# Revit family: Unterlegplatte_PLF_41_8_10_12_ FT_FTK
name_source: partatom
category: Generic Models
revit_build: Autodesk Revit 2017 (Build: 20160225_1515(x64)
units: mm (PartAtom-declared; Revit-internal decimal feet)

## family parameters
Always vertical = Yes
Can host rebar = No
Cut with Voids When Loaded = No
Part Type = Normal
Room Calculation Point = No
Round Connector Dimension = Use Diameter
Shared = No
Work Plane-Based = No

## types (4) — shared parameters
Manufacturer = OBO Bettermann
URL = http:/www.obo-bettermann.com

## per-type parameters (varying)
| type | Diameter | GTIN | Manufacturer Art.No. | Material |
| PLF 41 8 FT | 9 mm  [stored 0.0295276 ft] | 4012196675289 | 7207052 | Hot-dip galvanised |
| PLF 41 10 FT | 12 mm  [stored 0.0393701 ft] | 4012196675296 | 7207054 | Hot-dip galvanised |
| PLF 41 12 FT | 13 mm | 4012196675302 | 7207056 | Hot-dip galvanised |
| WBDHE 41 FTK | 12 mm  [stored 0.0393701 ft] | 4012196116867 | 1123192 | Steel |

note: column(s) folded — value = type name in every type: Article Type

note: [stored X ft] marks values corroborated as IEEE doubles in the binary element streams (Revit-internal decimal feet)

## geometry (parser evidence)
native form markers: Sweep x2
no freeform markers — native parametric forms only
